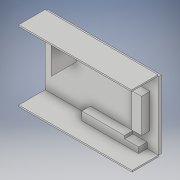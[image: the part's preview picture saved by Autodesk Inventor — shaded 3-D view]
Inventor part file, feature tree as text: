
AUTODESK INVENTOR PART (.ipt)
format: ipt  version: 2019 (Build 230136000, 136)  size: 177,152 bytes
history: native  units: in
note: dims shown in document units (in); Inventor stores cm internally (conversion verified against a paired STEP export)
features: extrude x7, sketch x7
ambient origin geometry x8: Origin, YZ Plane, XZ Plane, XY Plane, X Axis, Y Axis, Z Axis, Center Point
bodies: Solid1 (feature_tree)
feature tree (14):
  extrude  "Floor"  Depth=288.0in
  extrude  "Desk"  Depth=36.0in
  extrude  "Sinks"  Depth=42.0in
  extrude  "Counters"  Depth=36.0in TaperAngle=0.0deg
  extrude  "Room Walls"  Depth=60.0in
  extrude  "Roof"  TaperAngle=0.0deg  [1 undecoded]
  extrude  "Extrusion7"  Depth=36.0in
  sketch  "Sketch1"  dims[d0=480.0in d1=288.0in]
  sketch  "Sketch2"  dims[d2=12.0in d3=0.0in d4=36.0in]
  sketch  "Sketch3"  dims[d5=72.0in d6=42.0in]
  sketch  "Sketch4"  dims[d7=144.0in d8=36.0in d9=0.0in]
  sketch  "Sketch5"  dims[d10=24.0in d11=60.0in]
  sketch  "Sketch6"  dims[d12=48.0in d13=0.0in]
  sketch  "Sketch7"  dims[d14=36.0in d15=0.0in d16=36.0in d17=240.0in d18=180.0in d19=36.0in d20=36.0in d21=0.0in d22=6.0in d23=6.0in d24=112.0in d25=0.0in d26=6.0in d27=288.0in d28=0.0in d29=0.0312in d30=120.0in d31=106.0in d32=0.0in]
note: 1 required parameter value undecoded (feature->parameter linkage not recoverable at this tier; creation-order binding heuristic only, values carry confidence <= 0.55)
